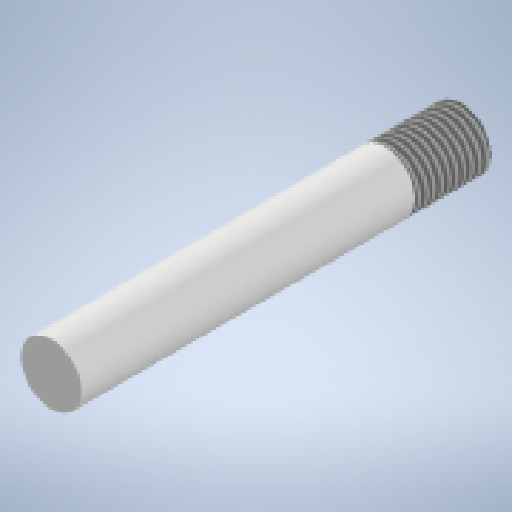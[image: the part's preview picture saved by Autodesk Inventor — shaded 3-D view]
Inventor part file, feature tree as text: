
AUTODESK INVENTOR PART (.ipt)
format: ipt  version: 2023 (Build 270158000, 158)  size: 140,800 bytes
history: native  units: mm
features: extrude x1, thread x1, sketch x1
ambient origin geometry x8: Origin, YZ Plane, XZ Plane, XY Plane, X Axis, Y Axis, Z Axis, Center Point
bodies: Solid1 (feature_tree)
feature tree (3):
  extrude  "Extrusion1"  Depth=27.0mm TaperAngle=0.0deg
  thread  "Thread1"  [1 undecoded]
  sketch  "Sketch1"  dims[d0=4.0mm d1=27.0mm d2=0.0mm d3=5.0mm d4=0.0mm]
note: 1 required parameter value undecoded (feature->parameter linkage not recoverable at this tier; creation-order binding heuristic only, values carry confidence <= 0.55)
